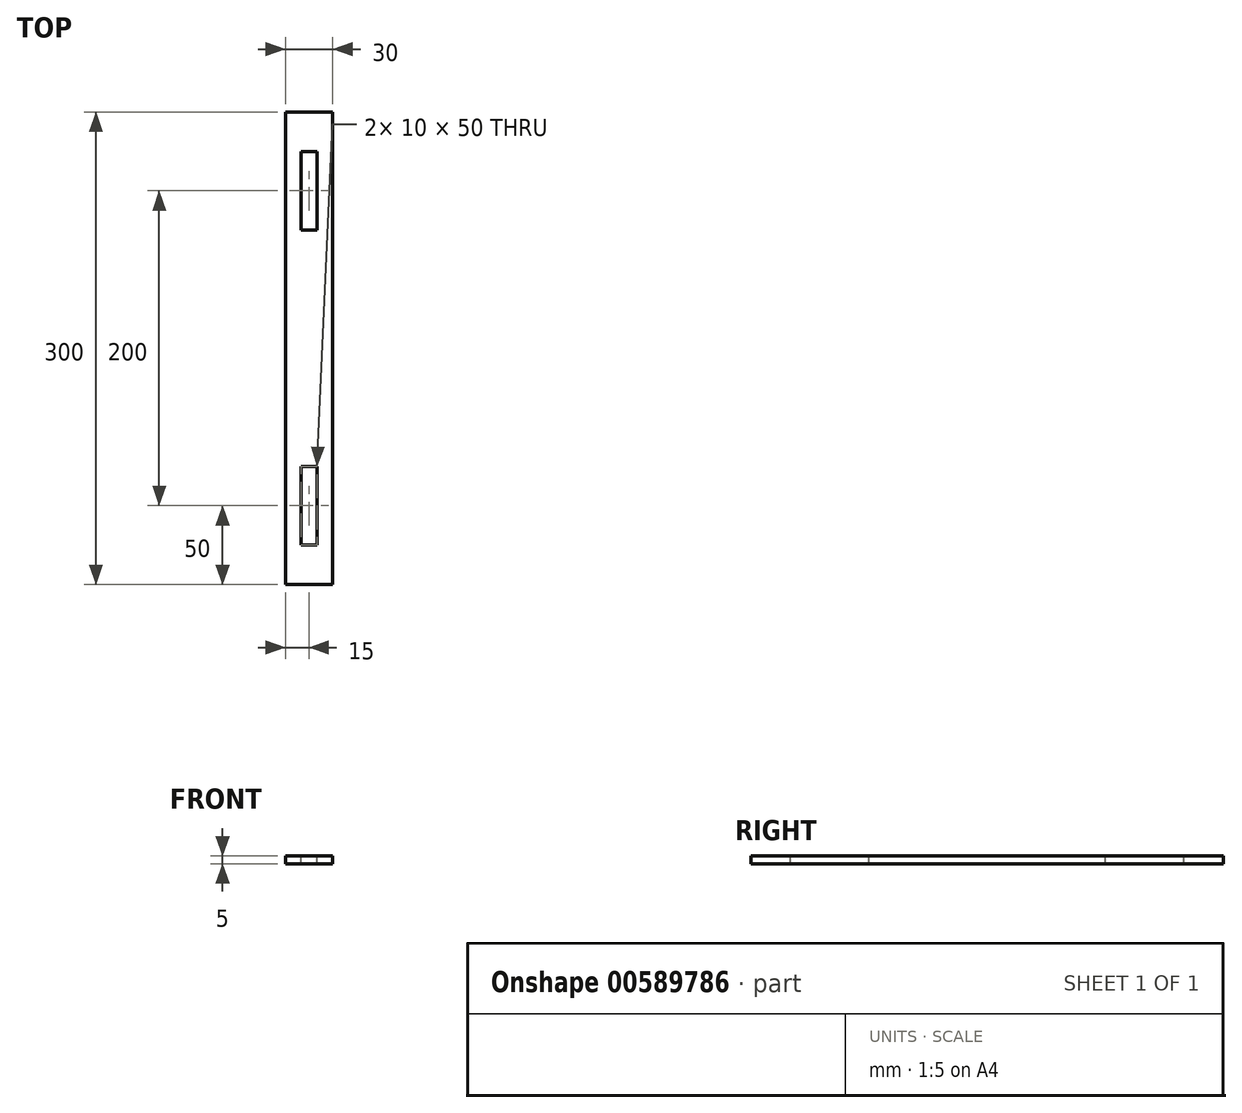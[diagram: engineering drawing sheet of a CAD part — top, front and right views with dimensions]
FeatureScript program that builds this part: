
annotation { "Feature Type Name" : "Feature", "Feature Type Description" : "" }
export const myFeature = defineFeature(function(context is Context, id is Id, definition is map)
    precondition{}
    {
        {
            var Q0;
            Q0=qCreatedBy(makeId("Top.planeOp"),FACE);
            var sketch = newSketch(context, id + "F0", { "sketchPlane" : qUnion([Q0])});
            skLineSegment(sketch, "E0.bottom", {"start": v(15, -150) * mm, "end": v(-15, -150) * mm});
            skLineSegment(sketch, "E0.top", {"start": v(15, 150) * mm, "end": v(-15, 150) * mm});
            skLineSegment(sketch, "E0.left", {"start": v(15, -150) * mm, "end": v(15, 150) * mm});
            skLineSegment(sketch, "E0.right", {"start": v(-15, -150) * mm, "end": v(-15, 150) * mm});
            skPoint(sketch, "E0.middle", {"position": v(0, 0) * mm});
            skPoint(sketch, "E1.middle", {"position": v(0, 150) * mm});
            skLineSegment(sketch, "E2.bottom", {"start": v(-15, 150) * mm, "end": v(-7.5, 150) * mm});
            skLineSegment(sketch, "E2.top", {"start": v(-15, 155) * mm, "end": v(-7.5, 155) * mm});
            skLineSegment(sketch, "E2.left", {"start": v(-15, 150) * mm, "end": v(-15, 155) * mm});
            skLineSegment(sketch, "E2.right", {"start": v(-7.5, 150) * mm, "end": v(-7.5, 155) * mm});
            skLineSegment(sketch, "E3.bottom", {"start": v(15, 150) * mm, "end": v(7.5, 150) * mm});
            skLineSegment(sketch, "E3.top", {"start": v(15, 155) * mm, "end": v(7.5, 155) * mm});
            skLineSegment(sketch, "E3.left", {"start": v(15, 150) * mm, "end": v(15, 155) * mm});
            skLineSegment(sketch, "E3.right", {"start": v(7.5, 150) * mm, "end": v(7.5, 155) * mm});
            skLineSegment(sketch, "E4.bottom", {"start": v(-15, -150) * mm, "end": v(-7.5, -150) * mm});
            skLineSegment(sketch, "E4.top", {"start": v(-15, -155) * mm, "end": v(-7.5, -155) * mm});
            skLineSegment(sketch, "E4.left", {"start": v(-15, -150) * mm, "end": v(-15, -155) * mm});
            skLineSegment(sketch, "E4.right", {"start": v(-7.5, -150) * mm, "end": v(-7.5, -155) * mm});
            skLineSegment(sketch, "E5.bottom", {"start": v(15, -150) * mm, "end": v(7.5, -150) * mm});
            skLineSegment(sketch, "E5.top", {"start": v(15, -155) * mm, "end": v(7.5, -155) * mm});
            skLineSegment(sketch, "E5.left", {"start": v(15, -150) * mm, "end": v(15, -155) * mm});
            skLineSegment(sketch, "E5.right", {"start": v(7.5, -150) * mm, "end": v(7.5, -155) * mm});
            skSolve(sketch);
        }
        {
            var Q0;
            Q0=makeQuery(id+"F0.imprint","IMPRINT",FACE,{"disambiguationData":[TD([[makeQuery(id+"F0.imprint","IMPRINT",EDGE,{"derivedFrom":sQuery(id+"F0.wireOp",EDGE,"E0.bottom")}),-1.0]])]});
            var Q1;
            Q1=makeQuery(id+"F0.imprint","IMPRINT",FACE,{"disambiguationData":[TD([[makeQuery(id+"F0.imprint","IMPRINT",EDGE,{"derivedFrom":sQuery(id+"F0.wireOp",EDGE,"E4.bottom")}),-1.0]])]});
            var Q2;
            Q2=makeQuery(id+"F0.imprint","IMPRINT",FACE,{"disambiguationData":[TD([[makeQuery(id+"F0.imprint","IMPRINT",EDGE,{"derivedFrom":sQuery(id+"F0.wireOp",EDGE,"E3.bottom")}),-1.0]])]});
            var Q3;
            Q3=makeQuery(id+"F0.imprint","IMPRINT",FACE,{"disambiguationData":[TD([[makeQuery(id+"F0.imprint","IMPRINT",EDGE,{"derivedFrom":sQuery(id+"F0.wireOp",EDGE,"E2.bottom")}),1.0]])]});
            var Q4;
            Q4=makeQuery(id+"F0.imprint","IMPRINT",FACE,{"disambiguationData":[TD([[makeQuery(id+"F0.imprint","IMPRINT",EDGE,{"derivedFrom":sQuery(id+"F0.wireOp",EDGE,"E5.bottom")}),1.0]])]});
            extrude(context, id + "F1", {"entities" : qUnion([Q0, Q1, Q2, Q3, Q4]), "endBound" : BoundingType.SYMMETRIC, "depth" : 5 * mm, "offsetDistance" : 25 * mm});
        }
        {
            var Q0;
            Q0=makeQuery(id+"F1.opExtrude","CAP_FACE",FACE,{"disambiguationData":[OSD([sQuery(id+"F0.wireOp",EDGE,"E0.bottom"),sQuery(id+"F0.wireOp",EDGE,"E0.top"),sQuery(id+"F0.wireOp",EDGE,"E0.left"),sQuery(id+"F0.wireOp",EDGE,"E0.right"),sQuery(id+"F0.wireOp",EDGE,"E2.top"),sQuery(id+"F0.wireOp",EDGE,"E2.left"),sQuery(id+"F0.wireOp",EDGE,"E2.right"),sQuery(id+"F0.wireOp",EDGE,"E3.top"),sQuery(id+"F0.wireOp",EDGE,"E3.left"),sQuery(id+"F0.wireOp",EDGE,"E3.right"),sQuery(id+"F0.wireOp",EDGE,"E4.top"),sQuery(id+"F0.wireOp",EDGE,"E4.left"),sQuery(id+"F0.wireOp",EDGE,"E4.right"),sQuery(id+"F0.wireOp",EDGE,"E5.top"),sQuery(id+"F0.wireOp",EDGE,"E5.left"),sQuery(id+"F0.wireOp",EDGE,"E5.right")])],"isStart":false});
            var sketch = newSketch(context, id + "F2", { "sketchPlane" : qUnion([Q0])});
            skLineSegment(sketch, "E6.bottom", {"start": v(5, -75) * mm, "end": v(-5, -75) * mm});
            skLineSegment(sketch, "E6.top", {"start": v(5, -125) * mm, "end": v(-5, -125) * mm});
            skLineSegment(sketch, "E6.left", {"start": v(5, -75) * mm, "end": v(5, -125) * mm});
            skLineSegment(sketch, "E6.right", {"start": v(-5, -75) * mm, "end": v(-5, -125) * mm});
            skPoint(sketch, "E6.middle", {"position": v(0, -100) * mm});
            skSolve(sketch);
        }
        {
            var Q0;
            Q0=makeQuery(id+"F2.imprint","IMPRINT",FACE,{"disambiguationData":[TD([[makeQuery(id+"F2.imprint","IMPRINT",EDGE,{"derivedFrom":sQuery(id+"F2.wireOp",EDGE,"E6.bottom")}),1.0]])]});
            extrude(context, id + "F3", {"entities" : qUnion([Q0]), "operationType" : NewBodyOperationType.REMOVE, "oppositeDirection" : true, "depth" : 10 * mm, "offsetDistance" : 25 * mm});
        }
        {
            var Q0;
            Q0=makeQuery(id+"F1.opExtrude","CAP_FACE",FACE,{"disambiguationData":[OSD([sQuery(id+"F0.wireOp",EDGE,"E0.bottom"),sQuery(id+"F0.wireOp",EDGE,"E0.top"),sQuery(id+"F0.wireOp",EDGE,"E0.left"),sQuery(id+"F0.wireOp",EDGE,"E0.right"),sQuery(id+"F0.wireOp",EDGE,"E2.top"),sQuery(id+"F0.wireOp",EDGE,"E2.left"),sQuery(id+"F0.wireOp",EDGE,"E2.right"),sQuery(id+"F0.wireOp",EDGE,"E3.top"),sQuery(id+"F0.wireOp",EDGE,"E3.left"),sQuery(id+"F0.wireOp",EDGE,"E3.right"),sQuery(id+"F0.wireOp",EDGE,"E4.top"),sQuery(id+"F0.wireOp",EDGE,"E4.left"),sQuery(id+"F0.wireOp",EDGE,"E4.right"),sQuery(id+"F0.wireOp",EDGE,"E5.top"),sQuery(id+"F0.wireOp",EDGE,"E5.left"),sQuery(id+"F0.wireOp",EDGE,"E5.right")])],"isStart":false});
            var sketch = newSketch(context, id + "F4", { "sketchPlane" : qUnion([Q0])});
            skLineSegment(sketch, "E7.bottom", {"start": v(5, 125) * mm, "end": v(-5, 125) * mm});
            skLineSegment(sketch, "E7.top", {"start": v(5, 75) * mm, "end": v(-5, 75) * mm});
            skLineSegment(sketch, "E7.left", {"start": v(5, 125) * mm, "end": v(5, 75) * mm});
            skLineSegment(sketch, "E7.right", {"start": v(-5, 125) * mm, "end": v(-5, 75) * mm});
            skPoint(sketch, "E7.middle", {"position": v(0, 100) * mm});
            skSolve(sketch);
        }
        {
            var Q0;
            Q0=makeQuery(id+"F4.imprint","IMPRINT",FACE,{"disambiguationData":[TD([[makeQuery(id+"F4.imprint","IMPRINT",EDGE,{"derivedFrom":sQuery(id+"F4.wireOp",EDGE,"E7.bottom")}),1.0]])]});
            extrude(context, id + "F5", {"entities" : qUnion([Q0]), "operationType" : NewBodyOperationType.REMOVE, "oppositeDirection" : true, "depth" : 10 * mm, "offsetDistance" : 25 * mm});
        }
    });
